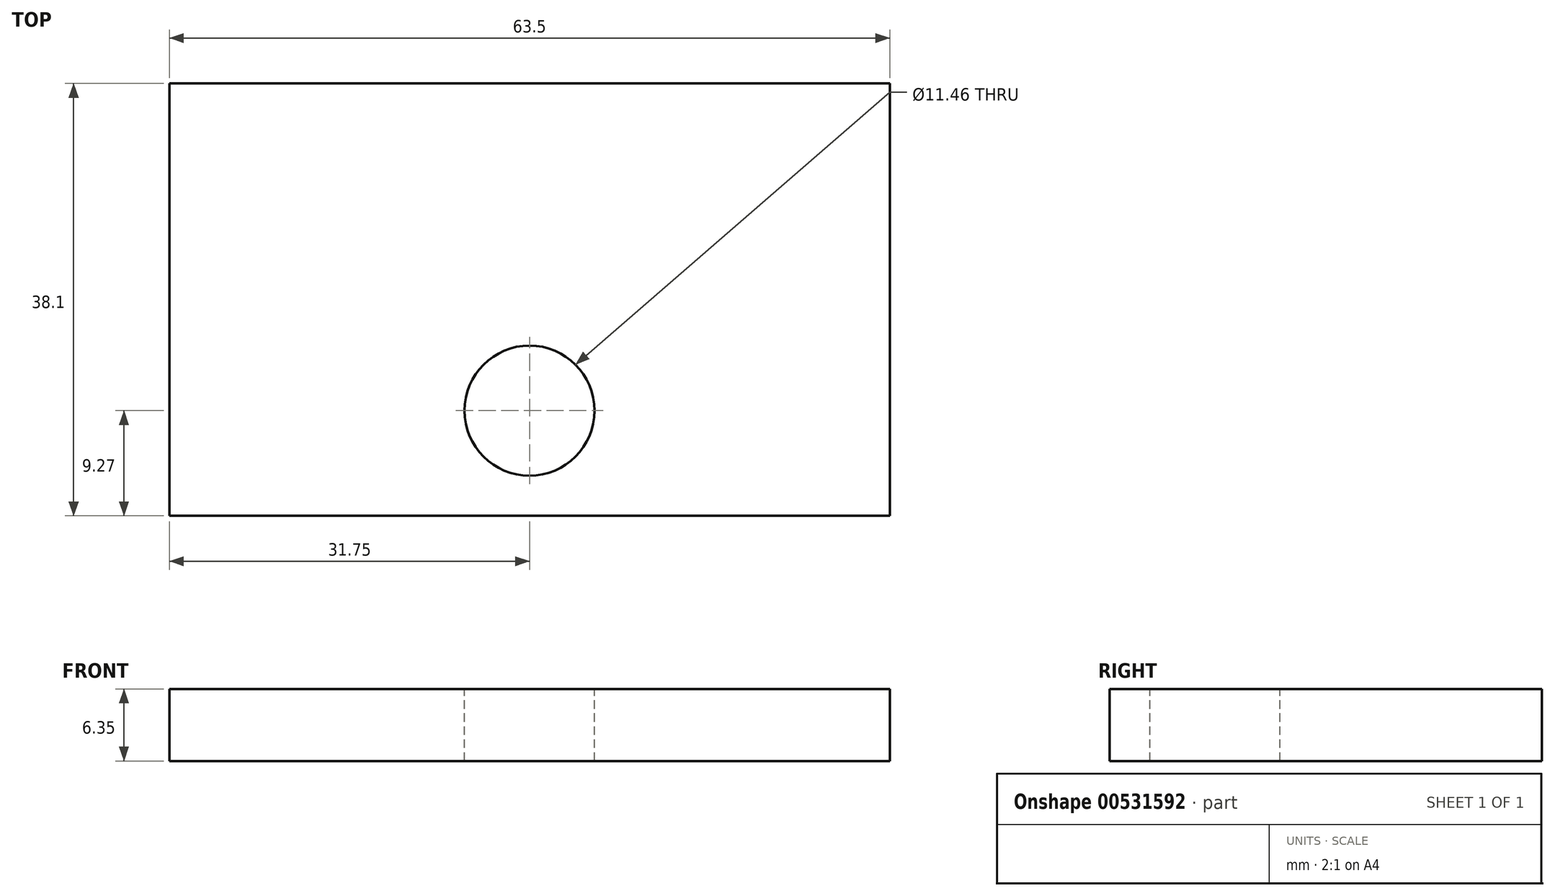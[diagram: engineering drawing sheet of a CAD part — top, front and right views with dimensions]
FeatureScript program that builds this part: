
annotation { "Feature Type Name" : "Feature", "Feature Type Description" : "" }
export const myFeature = defineFeature(function(context is Context, id is Id, definition is map)
    precondition{}
    {
        {
            var Q0;
            Q0=qCreatedBy(makeId("Top.planeOp"),FACE);
            var sketch = newSketch(context, id + "F0", { "sketchPlane" : qUnion([Q0])});
            skLineSegment(sketch, "E0.bottom", {"start": v(-31.75, -19.05) * mm, "end": v(31.75, -19.05) * mm});
            skLineSegment(sketch, "E0.top", {"start": v(-31.75, 19.05) * mm, "end": v(31.75, 19.05) * mm});
            skLineSegment(sketch, "E0.left", {"start": v(-31.75, -19.05) * mm, "end": v(-31.75, 19.05) * mm});
            skLineSegment(sketch, "E0.right", {"start": v(31.75, -19.05) * mm, "end": v(31.75, 19.05) * mm});
            skPoint(sketch, "E0.middle", {"position": v(0, 0) * mm});
            skSolve(sketch);
        }
        {
            var Q0;
            Q0=makeQuery(id+"F0.imprint","IMPRINT",FACE,{"disambiguationData":[TD([[makeQuery(id+"F0.imprint","IMPRINT",EDGE,{"derivedFrom":sQuery(id+"F0.wireOp",EDGE,"E0.bottom")}),1.0]])]});
            extrude(context, id + "F1", {"entities" : qUnion([Q0]), "depth" : 6.35 * mm, "offsetDistance" : 25.4 * mm});
        }
        {
            var Q0;
            Q0=makeQuery(id+"F1.opExtrude","CAP_FACE",FACE,{"disambiguationData":[OSD([sQuery(id+"F0.wireOp",EDGE,"E0.bottom"),sQuery(id+"F0.wireOp",EDGE,"E0.top"),sQuery(id+"F0.wireOp",EDGE,"E0.left"),sQuery(id+"F0.wireOp",EDGE,"E0.right")])],"isStart":false});
            var sketch = newSketch(context, id + "F2", { "sketchPlane" : qUnion([Q0])});
            skSolve(sketch);
        }
        {
            var Q0;
            Q0=makeQuery(id+"F2.imprint","IMPRINT",FACE,{"disambiguationData":[TD([[makeQuery(id+"F2.imprint","IMPRINT",EDGE,{"derivedFrom":makeQuery(id+"F1.opExtrude","CAP_EDGE",EDGE,{"disambiguationData":[OSD([sQuery(id+"F0.wireOp",EDGE,"E0.bottom")])],"isStart":false})}),1.0]])]});
            var sketch = newSketch(context, id + "F3", { "sketchPlane" : qUnion([Q0])});
            skCircle(sketch, "E1", {"center": v(0, -9.78) * mm, "radius": 5.73 * mm});
            skSolve(sketch);
        }
        {
            var Q0;
            Q0=makeQuery(id+"F3.imprint","IMPRINT",FACE,{"disambiguationData":[TD([[makeQuery(id+"F3.imprint","IMPRINT",EDGE,{"derivedFrom":sQuery(id+"F3.wireOp",EDGE,"E1")}),1.0]])]});
            var Q1;
            Q1=sQuery(id+"F3.wireOp",EDGE,"E1");
            extrude(context, id + "F4", {"entities" : qUnion([Q0]), "operationType" : NewBodyOperationType.REMOVE, "surfaceEntities" : qUnion([Q1]), "oppositeDirection" : true, "depth" : 51.05 * mm, "offsetDistance" : 25.4 * mm});
        }
    });
